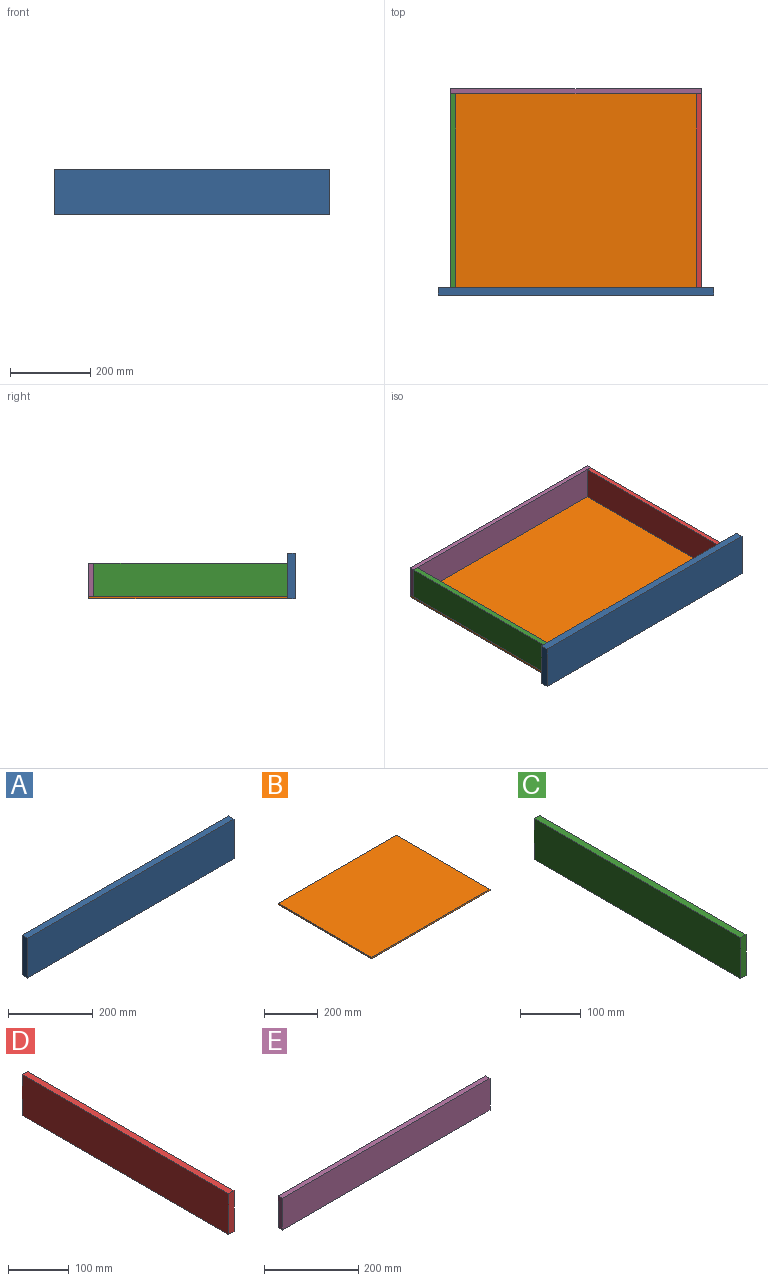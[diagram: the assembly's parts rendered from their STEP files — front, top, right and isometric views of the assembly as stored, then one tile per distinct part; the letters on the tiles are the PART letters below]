
ASSEMBLY  parts=5 mates=4
PART A: 6 faces, bbox 686.8x18.8x114.3 mm
  f0: plane 114.3x18.8mm, normal (1,0,0), area 2148.4mm2, adj f1,f3,f4,f5
  f1: plane 686.82x18.8mm, normal (0,0,1), area 12909.4mm2, adj f0,f2,f4,f5
  f2: plane 114.3x18.8mm, normal (-1,0,0), area 2148.4mm2, adj f1,f3,f4,f5
  f3: plane 686.82x18.8mm, normal (0,0,-1), area 12909.4mm2, adj f0,f2,f4,f5
  f4: plane 686.82x114.3mm, normal (0,-1,0), area 78503.1mm2, adj f0,f1,f2,f3
  f5: plane 686.82x114.3mm, normal (0,1,0), area 78503.1mm2, adj f0,f1,f2,f3
PART B: 6 faces, bbox 623.8x495.3x6.4 mm
  f0: plane 623.82x6.35mm, normal (0,1,0), area 3961.3mm2, adj f1,f3,f4,f5
  f1: plane 495.3x6.35mm, normal (-1,0,0), area 3145.2mm2, adj f0,f2,f4,f5
  f2: plane 623.82x6.35mm, normal (0,-1,0), area 3961.3mm2, adj f1,f3,f4,f5
  f3: plane 495.3x6.35mm, normal (1,0,0), area 3145.2mm2, adj f0,f2,f4,f5
  f4: plane 623.82x495.3mm, normal (0,0,1), area 308980mm2, adj f0,f1,f2,f3
  f5: plane 623.82x495.3mm, normal (0,0,-1), area 308980mm2, adj f0,f1,f2,f3
PART C: 6 faces, bbox 12.7x482.6x82.6 mm
  f0: plane 482.6x82.55mm, normal (1,0,0), area 39838.6mm2, adj f1,f3,f4,f5
  f1: plane 82.55x12.7mm, normal (0,1,0), area 1048.4mm2, adj f0,f2,f4,f5
  f2: plane 482.6x82.55mm, normal (-1,0,0), area 39838.6mm2, adj f1,f3,f4,f5
  f3: plane 82.55x12.7mm, normal (0,-1,0), area 1048.4mm2, adj f0,f2,f4,f5
  f4: plane 482.6x12.7mm, normal (0,0,1), area 6129mm2, adj f0,f1,f2,f3
  f5: plane 482.6x12.7mm, normal (0,0,-1), area 6129mm2, adj f0,f1,f2,f3
PART D: 6 faces, bbox 12.7x482.6x82.6 mm
  f0: plane 82.55x12.7mm, normal (0,1,0), area 1048.4mm2, adj f1,f3,f4,f5
  f1: plane 482.6x82.55mm, normal (-1,0,0), area 39838.6mm2, adj f0,f2,f4,f5
  f2: plane 82.55x12.7mm, normal (0,-1,0), area 1048.4mm2, adj f1,f3,f4,f5
  f3: plane 482.6x82.55mm, normal (1,0,0), area 39838.6mm2, adj f0,f2,f4,f5
  f4: plane 482.6x12.7mm, normal (0,0,1), area 6129mm2, adj f0,f1,f2,f3
  f5: plane 482.6x12.7mm, normal (0,0,-1), area 6129mm2, adj f0,f1,f2,f3
PART E: 6 faces, bbox 623.8x12.7x82.6 mm
  f0: plane 623.82x12.7mm, normal (0,0,1), area 7922.6mm2, adj f1,f3,f4,f5
  f1: plane 623.82x82.55mm, normal (0,-1,0), area 51496.7mm2, adj f0,f2,f3,f4
  f2: plane 623.82x12.7mm, normal (0,0,-1), area 7922.6mm2, adj f1,f3,f4,f5
  f3: plane 82.55x12.7mm, normal (1,0,0), area 1048.4mm2, adj f0,f1,f2,f5
  f4: plane 82.55x12.7mm, normal (-1,0,0), area 1048.4mm2, adj f0,f1,f2,f5
  f5: plane 623.82x82.55mm, normal (0,1,0), area 51496.7mm2, adj f0,f2,f3,f4
PLACE A t=(61.41,-54.79,14.9)mm
PLACE B t=(61.41,-54.79,8.55)mm
PLACE C t=(61.41,-54.79,8.55)mm
PLACE D t=(61.41,-54.79,8.55)mm
PLACE E t=(61.41,-54.79,8.55)mm
MATE fastened D.f3 <-> E.f3  axis (1,0,0) through (373.32,-98.99,541.95)mm
MATE fastened C.f2 <-> E.f4  axis (-1,0,0) through (-250.51,-98.99,541.95)mm
MATE fastened B.f1 <-> E.f4  axis (-1,0,0) through (-250.51,-86.29,541.95)mm
MATE fastened B.f2 <-> A.f5  axis (0,-1,0) through (61.41,-581.59,535.6)mm
